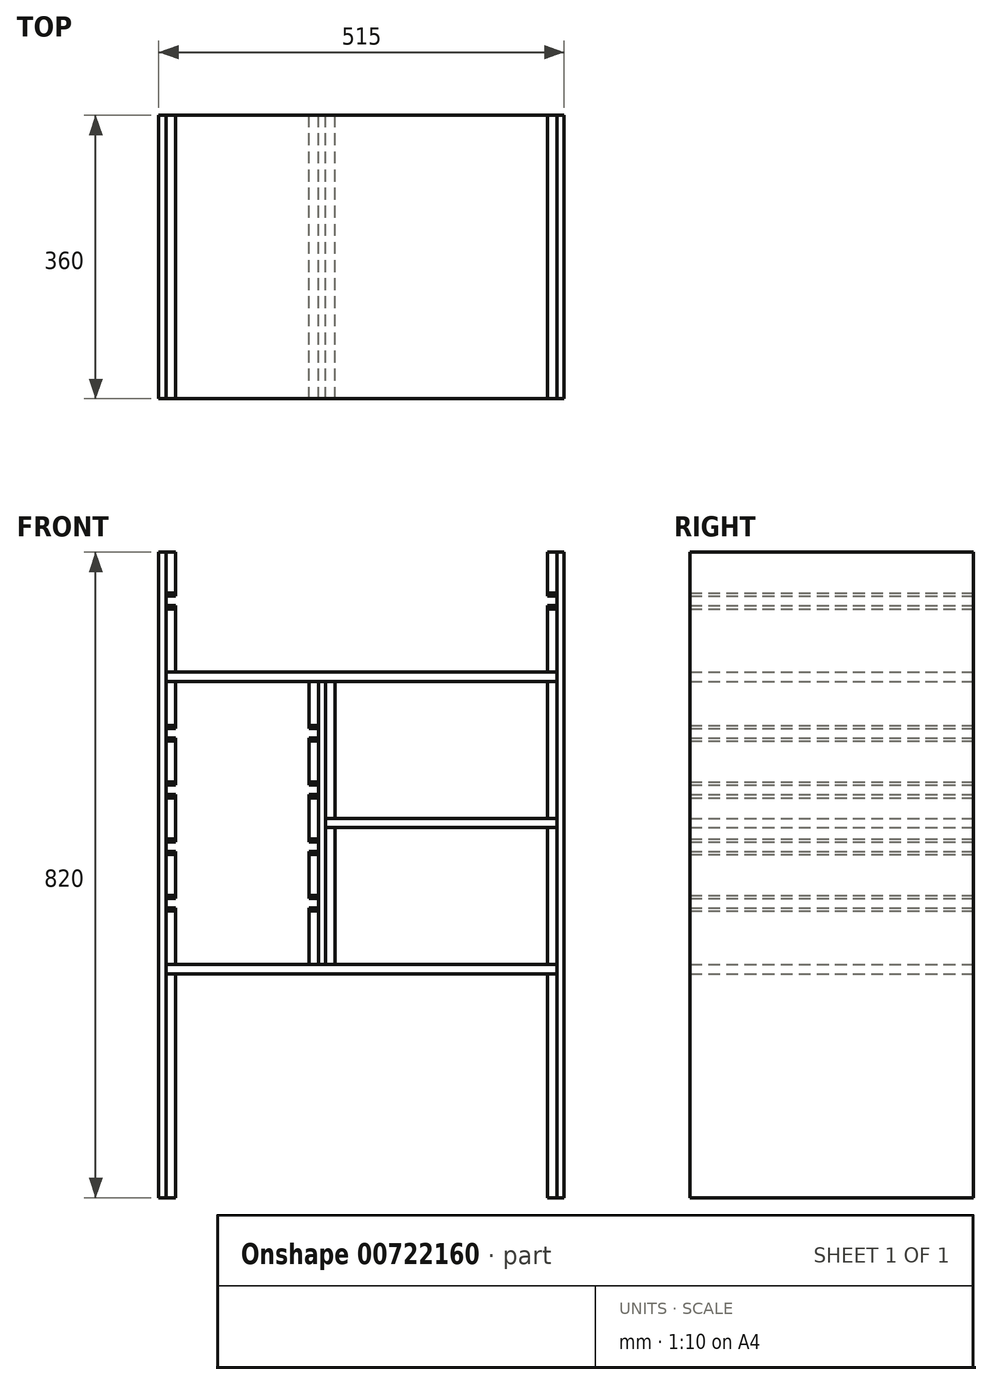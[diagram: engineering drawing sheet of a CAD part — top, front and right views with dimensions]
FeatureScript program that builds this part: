
annotation { "Feature Type Name" : "Feature", "Feature Type Description" : "" }
export const myFeature = defineFeature(function(context is Context, id is Id, definition is map)
    precondition{}
    {
        {
            var Q0;
            Q0=qCreatedBy(makeId("Front.planeOp"),FACE);
            var sketch = newSketch(context, id + "F0", { "sketchPlane" : qUnion([Q0])});
            skLineSegment(sketch, "E0.bottom", {"start": v(-175.37, 639.94) * mm, "end": v(-166.37, 639.94) * mm});
            skLineSegment(sketch, "E0.top", {"start": v(-175.37, -180.06) * mm, "end": v(-166.37, -180.06) * mm});
            skLineSegment(sketch, "E0.left", {"start": v(-175.37, 639.94) * mm, "end": v(-175.37, -180.06) * mm});
            skLineSegment(sketch, "E0.right", {"start": v(-166.37, 639.94) * mm, "end": v(-166.37, -180.06) * mm});
            skLineSegment(sketch, "E1.bottom", {"start": v(330.63, 639.94) * mm, "end": v(339.63, 639.94) * mm});
            skLineSegment(sketch, "E1.top", {"start": v(330.63, -180.06) * mm, "end": v(339.63, -180.06) * mm});
            skLineSegment(sketch, "E1.left", {"start": v(330.63, 639.94) * mm, "end": v(330.63, -180.06) * mm});
            skLineSegment(sketch, "E1.right", {"start": v(339.63, 639.94) * mm, "end": v(339.63, -180.06) * mm});
            skLineSegment(sketch, "E2", {"start": v(-166.37, 487.94) * mm, "end": v(330.63, 487.94) * mm});
            skLineSegment(sketch, "E3", {"start": v(-166.37, 475.94) * mm, "end": v(330.63, 475.94) * mm});
            skLineSegment(sketch, "E4", {"start": v(-166.37, 115.94) * mm, "end": v(330.63, 115.94) * mm});
            skLineSegment(sketch, "E5", {"start": v(-166.37, 103.94) * mm, "end": v(330.63, 103.94) * mm});
            skLineSegment(sketch, "E6", {"start": v(27.63, 475.94) * mm, "end": v(27.63, 115.94) * mm});
            skLineSegment(sketch, "E7", {"start": v(36.63, 475.94) * mm, "end": v(36.63, 115.94) * mm});
            skLineSegment(sketch, "E8", {"start": v(-154.37, 475.94) * mm, "end": v(-154.37, 419.94) * mm});
            skLineSegment(sketch, "E9", {"start": v(15.63, 475.94) * mm, "end": v(15.63, 419.94) * mm});
            skLineSegment(sketch, "E10", {"start": v(48.63, 475.94) * mm, "end": v(48.63, 301.94) * mm});
            skLineSegment(sketch, "E11", {"start": v(318.63, 475.94) * mm, "end": v(318.63, 301.94) * mm});
            skLineSegment(sketch, "E12", {"start": v(-154.37, 487.94) * mm, "end": v(-154.37, 567.94) * mm});
            skLineSegment(sketch, "E13", {"start": v(318.63, 487.94) * mm, "end": v(318.63, 567.94) * mm});
            skLineSegment(sketch, "E14", {"start": v(-154.37, 103.94) * mm, "end": v(-154.37, -180.06) * mm});
            skLineSegment(sketch, "E15", {"start": v(318.63, 103.94) * mm, "end": v(318.63, -180.06) * mm});
            skLineSegment(sketch, "E16", {"start": v(-166.37, 639.94) * mm, "end": v(-154.37, 639.94) * mm});
            skLineSegment(sketch, "E17", {"start": v(330.63, 639.94) * mm, "end": v(318.63, 639.94) * mm});
            skLineSegment(sketch, "E18", {"start": v(318.63, -180.06) * mm, "end": v(330.63, -180.06) * mm});
            skLineSegment(sketch, "E19", {"start": v(-154.37, -180.06) * mm, "end": v(-166.37, -180.06) * mm});
            skLineSegment(sketch, "E20", {"start": v(36.63, 301.94) * mm, "end": v(330.63, 301.94) * mm});
            skLineSegment(sketch, "E21", {"start": v(330.63, 289.94) * mm, "end": v(36.63, 289.94) * mm});
            skLineSegment(sketch, "E22.trimOffspring", {"start": v(48.63, 289.94) * mm, "end": v(48.63, 115.94) * mm});
            skLineSegment(sketch, "E23.trimOffspring", {"start": v(318.63, 289.94) * mm, "end": v(318.63, 115.94) * mm});
            skLineSegment(sketch, "E24", {"start": v(-154.37, 567.94) * mm, "end": v(-166.37, 567.94) * mm});
            skLineSegment(sketch, "E25", {"start": v(-154.37, 587.94) * mm, "end": v(-166.37, 587.94) * mm});
            skLineSegment(sketch, "E26", {"start": v(318.63, 587.94) * mm, "end": v(330.63, 587.94) * mm});
            skLineSegment(sketch, "E27", {"start": v(318.63, 567.94) * mm, "end": v(330.63, 567.94) * mm});
            skLineSegment(sketch, "E28.trimOffspring", {"start": v(-154.37, 587.94) * mm, "end": v(-154.37, 639.94) * mm});
            skLineSegment(sketch, "E29.trimOffspring", {"start": v(318.63, 587.94) * mm, "end": v(318.63, 639.94) * mm});
            skLineSegment(sketch, "E30", {"start": v(-154.37, 419.94) * mm, "end": v(-166.37, 419.94) * mm});
            skLineSegment(sketch, "E31", {"start": v(-154.37, 399.94) * mm, "end": v(-166.37, 399.94) * mm});
            skLineSegment(sketch, "E32", {"start": v(15.63, 419.94) * mm, "end": v(27.63, 419.94) * mm});
            skLineSegment(sketch, "E33", {"start": v(15.63, 399.94) * mm, "end": v(27.63, 399.94) * mm});
            skLineSegment(sketch, "E34", {"start": v(-166.37, 347.94) * mm, "end": v(-154.37, 347.94) * mm});
            skLineSegment(sketch, "E35", {"start": v(-166.37, 327.94) * mm, "end": v(-154.37, 327.94) * mm});
            skLineSegment(sketch, "E36", {"start": v(15.63, 347.94) * mm, "end": v(27.63, 347.94) * mm});
            skLineSegment(sketch, "E37", {"start": v(15.63, 327.94) * mm, "end": v(27.63, 327.94) * mm});
            skLineSegment(sketch, "E38", {"start": v(-166.37, 275.94) * mm, "end": v(-154.37, 275.94) * mm});
            skPoint(sketch, "E38.endSnap0", {"position": v(-154.37, 295.94) * mm});
            skLineSegment(sketch, "E39", {"start": v(-166.37, 255.94) * mm, "end": v(-154.37, 255.94) * mm});
            skLineSegment(sketch, "E40", {"start": v(15.63, 275.94) * mm, "end": v(27.63, 275.94) * mm});
            skLineSegment(sketch, "E41", {"start": v(15.63, 255.94) * mm, "end": v(27.63, 255.94) * mm});
            skLineSegment(sketch, "E42", {"start": v(-166.37, 203.94) * mm, "end": v(-154.37, 203.94) * mm});
            skLineSegment(sketch, "E43", {"start": v(-166.37, 183.94) * mm, "end": v(-154.37, 183.94) * mm});
            skLineSegment(sketch, "E44", {"start": v(15.63, 203.94) * mm, "end": v(27.63, 203.94) * mm});
            skLineSegment(sketch, "E45", {"start": v(15.63, 183.94) * mm, "end": v(27.63, 183.94) * mm});
            skLineSegment(sketch, "E46.trimOffspring", {"start": v(-154.37, 399.94) * mm, "end": v(-154.37, 347.94) * mm});
            skLineSegment(sketch, "E47.trimOffspring", {"start": v(-154.37, 327.94) * mm, "end": v(-154.37, 275.94) * mm});
            skLineSegment(sketch, "E48.trimOffspring", {"start": v(-154.37, 255.94) * mm, "end": v(-154.37, 203.94) * mm});
            skLineSegment(sketch, "E49.trimOffspring", {"start": v(-154.37, 183.94) * mm, "end": v(-154.37, 115.94) * mm});
            skLineSegment(sketch, "E50.trimOffspring", {"start": v(15.63, 183.94) * mm, "end": v(15.63, 115.94) * mm});
            skLineSegment(sketch, "E51.trimOffspring", {"start": v(15.63, 255.94) * mm, "end": v(15.63, 203.94) * mm});
            skLineSegment(sketch, "E52.trimOffspring", {"start": v(15.63, 327.94) * mm, "end": v(15.63, 275.94) * mm});
            skLineSegment(sketch, "E53.trimOffspring", {"start": v(15.63, 399.94) * mm, "end": v(15.63, 347.94) * mm});
            skLineSegment(sketch, "E54", {"start": v(-154.37, 419.94) * mm, "end": v(-154.37, 415.94) * mm});
            skLineSegment(sketch, "E55", {"start": v(-166.37, 415.94) * mm, "end": v(-154.37, 415.94) * mm});
            skLineSegment(sketch, "E56", {"start": v(-166.37, 403.94) * mm, "end": v(-154.37, 403.94) * mm});
            skLineSegment(sketch, "E57.trimOffspring", {"start": v(-154.37, 403.94) * mm, "end": v(-154.37, 399.94) * mm});
            skLineSegment(sketch, "E58", {"start": v(-154.37, 347.94) * mm, "end": v(-154.37, 343.94) * mm});
            skLineSegment(sketch, "E59", {"start": v(-154.37, 343.94) * mm, "end": v(-166.37, 343.94) * mm});
            skLineSegment(sketch, "E60", {"start": v(-154.37, 331.94) * mm, "end": v(-166.37, 331.94) * mm});
            skLineSegment(sketch, "E61", {"start": v(-154.37, 255.94) * mm, "end": v(-154.37, 259.94) * mm});
            skLineSegment(sketch, "E62", {"start": v(-166.37, 271.94) * mm, "end": v(-154.37, 271.94) * mm});
            skLineSegment(sketch, "E63", {"start": v(-166.37, 259.94) * mm, "end": v(-154.37, 259.94) * mm});
            skLineSegment(sketch, "E64", {"start": v(-154.37, 203.94) * mm, "end": v(-154.37, 199.94) * mm});
            skLineSegment(sketch, "E65", {"start": v(-154.37, 199.94) * mm, "end": v(-166.37, 199.94) * mm});
            skLineSegment(sketch, "E66", {"start": v(-166.37, 187.94) * mm, "end": v(-154.37, 187.94) * mm});
            skLineSegment(sketch, "E67", {"start": v(15.63, 419.94) * mm, "end": v(15.63, 415.94) * mm});
            skLineSegment(sketch, "E68", {"start": v(15.63, 327.94) * mm, "end": v(15.63, 331.94) * mm});
            skLineSegment(sketch, "E69", {"start": v(15.63, 275.94) * mm, "end": v(15.63, 271.94) * mm});
            skLineSegment(sketch, "E70", {"start": v(15.63, 203.94) * mm, "end": v(15.63, 199.94) * mm});
            skLineSegment(sketch, "E71", {"start": v(15.63, 415.94) * mm, "end": v(27.63, 415.94) * mm});
            skLineSegment(sketch, "E72", {"start": v(15.63, 403.94) * mm, "end": v(27.63, 403.94) * mm});
            skLineSegment(sketch, "E73", {"start": v(15.63, 343.94) * mm, "end": v(27.63, 343.94) * mm});
            skLineSegment(sketch, "E74", {"start": v(15.63, 331.94) * mm, "end": v(27.63, 331.94) * mm});
            skLineSegment(sketch, "E75", {"start": v(15.63, 259.94) * mm, "end": v(27.63, 259.94) * mm});
            skLineSegment(sketch, "E76", {"start": v(15.63, 271.94) * mm, "end": v(27.63, 271.94) * mm});
            skLineSegment(sketch, "E77", {"start": v(15.63, 187.94) * mm, "end": v(27.63, 187.94) * mm});
            skLineSegment(sketch, "E78", {"start": v(15.63, 199.94) * mm, "end": v(27.63, 199.94) * mm});
            skLineSegment(sketch, "E79.trimOffspring", {"start": v(-154.37, 187.94) * mm, "end": v(-154.37, 183.94) * mm});
            skLineSegment(sketch, "E80.trimOffspring", {"start": v(-154.37, 271.94) * mm, "end": v(-154.37, 275.94) * mm});
            skLineSegment(sketch, "E81.trimOffspring", {"start": v(15.63, 187.94) * mm, "end": v(15.63, 183.94) * mm});
            skLineSegment(sketch, "E82.trimOffspring", {"start": v(15.63, 259.94) * mm, "end": v(15.63, 255.94) * mm});
            skLineSegment(sketch, "E83.trimOffspring", {"start": v(15.63, 343.94) * mm, "end": v(15.63, 347.94) * mm});
            skLineSegment(sketch, "E84.trimOffspring", {"start": v(15.63, 403.94) * mm, "end": v(15.63, 399.94) * mm});
            skLineSegment(sketch, "E85.trimOffspring", {"start": v(-154.37, 331.94) * mm, "end": v(-154.37, 327.94) * mm});
            skLineSegment(sketch, "E86", {"start": v(-154.37, 587.94) * mm, "end": v(-154.37, 583.94) * mm});
            skLineSegment(sketch, "E87", {"start": v(-166.37, 583.94) * mm, "end": v(-154.37, 583.94) * mm});
            skLineSegment(sketch, "E88", {"start": v(-166.37, 571.94) * mm, "end": v(-154.37, 571.94) * mm});
            skPoint(sketch, "E88.endSnap0", {"position": v(-154.37, 577.94) * mm});
            skLineSegment(sketch, "E89", {"start": v(318.63, 587.94) * mm, "end": v(318.63, 583.94) * mm});
            skLineSegment(sketch, "E90", {"start": v(318.63, 583.94) * mm, "end": v(330.63, 583.94) * mm});
            skLineSegment(sketch, "E91", {"start": v(318.63, 571.94) * mm, "end": v(330.63, 571.94) * mm});
            skLineSegment(sketch, "E92.trimOffspring", {"start": v(318.63, 571.94) * mm, "end": v(318.63, 567.94) * mm});
            skLineSegment(sketch, "E93.trimOffspring", {"start": v(-154.37, 571.94) * mm, "end": v(-154.37, 567.94) * mm});
            skSolve(sketch);
        }
        {
            var Q0;
            {var subQ5=sQuery(id+"F0.wireOp",EDGE,"E0.right");var subQ8=sQuery(id+"F0.wireOp",EDGE,"E2");var subQ12=makeQuery(id+"F0.imprint","INTERSECT",VERTEX,{"derivedFrom":[subQ5,subQ8]});Q0=makeQuery(id+"F0.imprint","IMPRINT",FACE,{"disambiguationData":[TD([[makeQuery(id+"F0.imprint","IMPRINT",EDGE,{"disambiguationData":[TD([[subQ12,-1.0]])],"derivedFrom":subQ5}),1.0]])]});}
            var Q1;
            {var subQ1=sQuery(id+"F0.wireOp",EDGE,"E0.right");var subQ4=sQuery(id+"F0.wireOp",EDGE,"E4");var subQ13=makeQuery(id+"F0.imprint","INTERSECT",VERTEX,{"derivedFrom":[subQ1,subQ4]});Q1=makeQuery(id+"F0.imprint","IMPRINT",FACE,{"disambiguationData":[TD([[makeQuery(id+"F0.imprint","IMPRINT",EDGE,{"disambiguationData":[TD([[subQ13,-1.0]])],"derivedFrom":subQ1}),1.0]])]});}
            var Q2;
            {var subQ0=sQuery(id+"F0.wireOp",EDGE,"E33");Q2=makeQuery(id+"F0.imprint","IMPRINT",FACE,{"disambiguationData":[TD([[makeQuery(id+"F0.imprint","IMPRINT",EDGE,{"derivedFrom":subQ0}),-1.0]])]});}
            var Q3;
            {var subQ0=sQuery(id+"F0.wireOp",EDGE,"E37");Q3=makeQuery(id+"F0.imprint","IMPRINT",FACE,{"disambiguationData":[TD([[makeQuery(id+"F0.imprint","IMPRINT",EDGE,{"derivedFrom":subQ0}),-1.0]])]});}
            var Q4;
            {var subQ0=sQuery(id+"F0.wireOp",EDGE,"E41");Q4=makeQuery(id+"F0.imprint","IMPRINT",FACE,{"disambiguationData":[TD([[makeQuery(id+"F0.imprint","IMPRINT",EDGE,{"derivedFrom":subQ0}),-1.0]])]});}
            var Q5;
            {var subQ0=sQuery(id+"F0.wireOp",EDGE,"E39");Q5=makeQuery(id+"F0.imprint","IMPRINT",FACE,{"disambiguationData":[TD([[makeQuery(id+"F0.imprint","IMPRINT",EDGE,{"derivedFrom":subQ0}),-1.0]])]});}
            var Q6;
            {var subQ0=sQuery(id+"F0.wireOp",EDGE,"E35");Q6=makeQuery(id+"F0.imprint","IMPRINT",FACE,{"disambiguationData":[TD([[makeQuery(id+"F0.imprint","IMPRINT",EDGE,{"derivedFrom":subQ0}),-1.0]])]});}
            var Q7;
            {var subQ0=sQuery(id+"F0.wireOp",EDGE,"E31");Q7=makeQuery(id+"F0.imprint","IMPRINT",FACE,{"disambiguationData":[TD([[makeQuery(id+"F0.imprint","IMPRINT",EDGE,{"derivedFrom":subQ0}),1.0]])]});}
            var Q8;
            {var subQ0=sQuery(id+"F0.wireOp",EDGE,"E20");var subQ7=sQuery(id+"F0.wireOp",EDGE,"E1.left");var subQ8=makeQuery(id+"F0.imprint","INTERSECT",VERTEX,{"derivedFrom":[subQ7,subQ0]});Q8=makeQuery(id+"F0.imprint","IMPRINT",FACE,{"disambiguationData":[TD([[makeQuery(id+"F0.imprint","IMPRINT",EDGE,{"disambiguationData":[TD([[subQ8,-1.0]])],"derivedFrom":subQ7}),-1.0]])]});}
            var Q9;
            {var subQ0=sQuery(id+"F0.wireOp",EDGE,"E17");Q9=makeQuery(id+"F0.imprint","IMPRINT",FACE,{"disambiguationData":[TD([[makeQuery(id+"F0.imprint","IMPRINT",EDGE,{"derivedFrom":subQ0}),1.0]])]});}
            var Q10;
            {var subQ0=sQuery(id+"F0.wireOp",EDGE,"E16");Q10=makeQuery(id+"F0.imprint","IMPRINT",FACE,{"disambiguationData":[TD([[makeQuery(id+"F0.imprint","IMPRINT",EDGE,{"derivedFrom":subQ0}),-1.0]])]});}
            extrude(context, id + "F1", {"entities" : qUnion([Q0, Q1, Q2, Q3, Q4, Q5, Q6, Q7, Q8, Q9, Q10]), "depth" : 360 * mm, "offsetDistance" : 25 * mm});
        }
        {
            var Q0;
            {var subQ4=sQuery(id+"F0.wireOp",EDGE,"E12");Q0=makeQuery(id+"F0.imprint","IMPRINT",FACE,{"disambiguationData":[TD([[makeQuery(id+"F0.imprint","IMPRINT",EDGE,{"derivedFrom":subQ4}),1.0]])]});}
            var Q1;
            {var subQ4=sQuery(id+"F0.wireOp",EDGE,"E13");Q1=makeQuery(id+"F0.imprint","IMPRINT",FACE,{"disambiguationData":[TD([[makeQuery(id+"F0.imprint","IMPRINT",EDGE,{"derivedFrom":subQ4}),-1.0]])]});}
            var Q2;
            {var subQ5=sQuery(id+"F0.wireOp",EDGE,"E11");Q2=makeQuery(id+"F0.imprint","IMPRINT",FACE,{"disambiguationData":[TD([[makeQuery(id+"F0.imprint","IMPRINT",EDGE,{"derivedFrom":subQ5}),1.0]])]});}
            var Q3;
            {var subQ5=sQuery(id+"F0.wireOp",EDGE,"E23.trimOffspring");Q3=makeQuery(id+"F0.imprint","IMPRINT",FACE,{"disambiguationData":[TD([[makeQuery(id+"F0.imprint","IMPRINT",EDGE,{"derivedFrom":subQ5}),1.0]])]});}
            var Q4;
            {var subQ4=sQuery(id+"F0.wireOp",EDGE,"E15");Q4=makeQuery(id+"F0.imprint","IMPRINT",FACE,{"disambiguationData":[TD([[makeQuery(id+"F0.imprint","IMPRINT",EDGE,{"derivedFrom":subQ4}),1.0]])]});}
            var Q5;
            {var subQ3=sQuery(id+"F0.wireOp",EDGE,"E43");Q5=makeQuery(id+"F0.imprint","IMPRINT",FACE,{"disambiguationData":[TD([[makeQuery(id+"F0.imprint","IMPRINT",EDGE,{"derivedFrom":subQ3}),-1.0]])]});}
            var Q6;
            {var subQ4=sQuery(id+"F0.wireOp",EDGE,"E45");Q6=makeQuery(id+"F0.imprint","IMPRINT",FACE,{"disambiguationData":[TD([[makeQuery(id+"F0.imprint","IMPRINT",EDGE,{"derivedFrom":subQ4}),-1.0]])]});}
            var Q7;
            {var subQ4=sQuery(id+"F0.wireOp",EDGE,"E14");Q7=makeQuery(id+"F0.imprint","IMPRINT",FACE,{"disambiguationData":[TD([[makeQuery(id+"F0.imprint","IMPRINT",EDGE,{"derivedFrom":subQ4}),-1.0]])]});}
            var Q8;
            {var subQ4=sQuery(id+"F0.wireOp",EDGE,"E8");Q8=makeQuery(id+"F0.imprint","IMPRINT",FACE,{"disambiguationData":[TD([[makeQuery(id+"F0.imprint","IMPRINT",EDGE,{"derivedFrom":subQ4}),-1.0]])]});}
            var Q9;
            {var subQ3=sQuery(id+"F0.wireOp",EDGE,"E9");Q9=makeQuery(id+"F0.imprint","IMPRINT",FACE,{"disambiguationData":[TD([[makeQuery(id+"F0.imprint","IMPRINT",EDGE,{"derivedFrom":subQ3}),1.0]])]});}
            var Q10;
            {var subQ3=sQuery(id+"F0.wireOp",EDGE,"E10");Q10=makeQuery(id+"F0.imprint","IMPRINT",FACE,{"disambiguationData":[TD([[makeQuery(id+"F0.imprint","IMPRINT",EDGE,{"derivedFrom":subQ3}),-1.0]])]});}
            var Q11;
            {var subQ3=sQuery(id+"F0.wireOp",EDGE,"E22.trimOffspring");Q11=makeQuery(id+"F0.imprint","IMPRINT",FACE,{"disambiguationData":[TD([[makeQuery(id+"F0.imprint","IMPRINT",EDGE,{"derivedFrom":subQ3}),-1.0]])]});}
            extrude(context, id + "F2", {"entities" : qUnion([Q0, Q1, Q2, Q3, Q4, Q5, Q6, Q7, Q8, Q9, Q10, Q11]), "depth" : 360 * mm, "offsetDistance" : 25 * mm});
        }
        {
            var Q0;
            {var subQ8=sQuery(id+"F0.wireOp",EDGE,"E1.bottom");Q0=makeQuery(id+"F0.imprint","IMPRINT",FACE,{"disambiguationData":[TD([[makeQuery(id+"F0.imprint","IMPRINT",EDGE,{"derivedFrom":subQ8}),-1.0]])]});}
            var Q1;
            {var subQ8=sQuery(id+"F0.wireOp",EDGE,"E0.bottom");Q1=makeQuery(id+"F0.imprint","IMPRINT",FACE,{"disambiguationData":[TD([[makeQuery(id+"F0.imprint","IMPRINT",EDGE,{"derivedFrom":subQ8}),-1.0]])]});}
            var Q2;
            {var subQ0=sQuery(id+"F0.wireOp",EDGE,"E6");var subQ8=sQuery(id+"F0.wireOp",EDGE,"E3");var subQ9=makeQuery(id+"F0.imprint","INTERSECT",VERTEX,{"derivedFrom":[subQ8,subQ0]});Q2=makeQuery(id+"F0.imprint","IMPRINT",FACE,{"disambiguationData":[TD([[makeQuery(id+"F0.imprint","IMPRINT",EDGE,{"disambiguationData":[TD([[subQ9,-1.0]])],"derivedFrom":subQ8}),-1.0]])]});}
            extrude(context, id + "F3", {"entities" : qUnion([Q0, Q1, Q2]), "depth" : 360 * mm, "offsetDistance" : 25 * mm});
        }
        {
            var Q0;
            {var subQ0=sQuery(id+"F0.wireOp",EDGE,"E30");Q0=makeQuery(id+"F0.imprint","IMPRINT",FACE,{"disambiguationData":[TD([[makeQuery(id+"F0.imprint","IMPRINT",EDGE,{"derivedFrom":subQ0}),1.0]])]});}
            var Q1;
            {var subQ0=sQuery(id+"F0.wireOp",EDGE,"E31");Q1=makeQuery(id+"F0.imprint","IMPRINT",FACE,{"disambiguationData":[TD([[makeQuery(id+"F0.imprint","IMPRINT",EDGE,{"derivedFrom":subQ0}),-1.0]])]});}
            var Q2;
            {var subQ0=sQuery(id+"F0.wireOp",EDGE,"E34");Q2=makeQuery(id+"F0.imprint","IMPRINT",FACE,{"disambiguationData":[TD([[makeQuery(id+"F0.imprint","IMPRINT",EDGE,{"derivedFrom":subQ0}),-1.0]])]});}
            var Q3;
            {var subQ0=sQuery(id+"F0.wireOp",EDGE,"E35");Q3=makeQuery(id+"F0.imprint","IMPRINT",FACE,{"disambiguationData":[TD([[makeQuery(id+"F0.imprint","IMPRINT",EDGE,{"derivedFrom":subQ0}),1.0]])]});}
            var Q4;
            {var subQ0=sQuery(id+"F0.wireOp",EDGE,"E38");Q4=makeQuery(id+"F0.imprint","IMPRINT",FACE,{"disambiguationData":[TD([[makeQuery(id+"F0.imprint","IMPRINT",EDGE,{"derivedFrom":subQ0}),-1.0]])]});}
            var Q5;
            {var subQ0=sQuery(id+"F0.wireOp",EDGE,"E39");Q5=makeQuery(id+"F0.imprint","IMPRINT",FACE,{"disambiguationData":[TD([[makeQuery(id+"F0.imprint","IMPRINT",EDGE,{"derivedFrom":subQ0}),1.0]])]});}
            var Q6;
            {var subQ0=sQuery(id+"F0.wireOp",EDGE,"E42");Q6=makeQuery(id+"F0.imprint","IMPRINT",FACE,{"disambiguationData":[TD([[makeQuery(id+"F0.imprint","IMPRINT",EDGE,{"derivedFrom":subQ0}),-1.0]])]});}
            var Q7;
            {var subQ0=sQuery(id+"F0.wireOp",EDGE,"E43");Q7=makeQuery(id+"F0.imprint","IMPRINT",FACE,{"disambiguationData":[TD([[makeQuery(id+"F0.imprint","IMPRINT",EDGE,{"derivedFrom":subQ0}),1.0]])]});}
            var Q8;
            {var subQ0=sQuery(id+"F0.wireOp",EDGE,"E45");Q8=makeQuery(id+"F0.imprint","IMPRINT",FACE,{"disambiguationData":[TD([[makeQuery(id+"F0.imprint","IMPRINT",EDGE,{"derivedFrom":subQ0}),1.0]])]});}
            var Q9;
            {var subQ0=sQuery(id+"F0.wireOp",EDGE,"E44");Q9=makeQuery(id+"F0.imprint","IMPRINT",FACE,{"disambiguationData":[TD([[makeQuery(id+"F0.imprint","IMPRINT",EDGE,{"derivedFrom":subQ0}),-1.0]])]});}
            var Q10;
            {var subQ0=sQuery(id+"F0.wireOp",EDGE,"E40");Q10=makeQuery(id+"F0.imprint","IMPRINT",FACE,{"disambiguationData":[TD([[makeQuery(id+"F0.imprint","IMPRINT",EDGE,{"derivedFrom":subQ0}),-1.0]])]});}
            var Q11;
            {var subQ0=sQuery(id+"F0.wireOp",EDGE,"E41");Q11=makeQuery(id+"F0.imprint","IMPRINT",FACE,{"disambiguationData":[TD([[makeQuery(id+"F0.imprint","IMPRINT",EDGE,{"derivedFrom":subQ0}),1.0]])]});}
            var Q12;
            {var subQ0=sQuery(id+"F0.wireOp",EDGE,"E36");Q12=makeQuery(id+"F0.imprint","IMPRINT",FACE,{"disambiguationData":[TD([[makeQuery(id+"F0.imprint","IMPRINT",EDGE,{"derivedFrom":subQ0}),-1.0]])]});}
            var Q13;
            {var subQ0=sQuery(id+"F0.wireOp",EDGE,"E37");Q13=makeQuery(id+"F0.imprint","IMPRINT",FACE,{"disambiguationData":[TD([[makeQuery(id+"F0.imprint","IMPRINT",EDGE,{"derivedFrom":subQ0}),1.0]])]});}
            var Q14;
            {var subQ0=sQuery(id+"F0.wireOp",EDGE,"E32");Q14=makeQuery(id+"F0.imprint","IMPRINT",FACE,{"disambiguationData":[TD([[makeQuery(id+"F0.imprint","IMPRINT",EDGE,{"derivedFrom":subQ0}),-1.0]])]});}
            var Q15;
            {var subQ0=sQuery(id+"F0.wireOp",EDGE,"E33");Q15=makeQuery(id+"F0.imprint","IMPRINT",FACE,{"disambiguationData":[TD([[makeQuery(id+"F0.imprint","IMPRINT",EDGE,{"derivedFrom":subQ0}),1.0]])]});}
            var Q16;
            {var subQ0=sQuery(id+"F0.wireOp",EDGE,"E25");Q16=makeQuery(id+"F0.imprint","IMPRINT",FACE,{"disambiguationData":[TD([[makeQuery(id+"F0.imprint","IMPRINT",EDGE,{"derivedFrom":subQ0}),1.0]])]});}
            var Q17;
            {var subQ0=sQuery(id+"F0.wireOp",EDGE,"E24");Q17=makeQuery(id+"F0.imprint","IMPRINT",FACE,{"disambiguationData":[TD([[makeQuery(id+"F0.imprint","IMPRINT",EDGE,{"derivedFrom":subQ0}),-1.0]])]});}
            var Q18;
            {var subQ0=sQuery(id+"F0.wireOp",EDGE,"E26");Q18=makeQuery(id+"F0.imprint","IMPRINT",FACE,{"disambiguationData":[TD([[makeQuery(id+"F0.imprint","IMPRINT",EDGE,{"derivedFrom":subQ0}),-1.0]])]});}
            var Q19;
            {var subQ0=sQuery(id+"F0.wireOp",EDGE,"E27");Q19=makeQuery(id+"F0.imprint","IMPRINT",FACE,{"disambiguationData":[TD([[makeQuery(id+"F0.imprint","IMPRINT",EDGE,{"derivedFrom":subQ0}),1.0]])]});}
            extrude(context, id + "F4", {"entities" : qUnion([Q0, Q1, Q2, Q3, Q4, Q5, Q6, Q7, Q8, Q9, Q10, Q11, Q12, Q13, Q14, Q15, Q16, Q17, Q18, Q19]), "depth" : 360 * mm, "offsetDistance" : 25 * mm});
        }
    });
